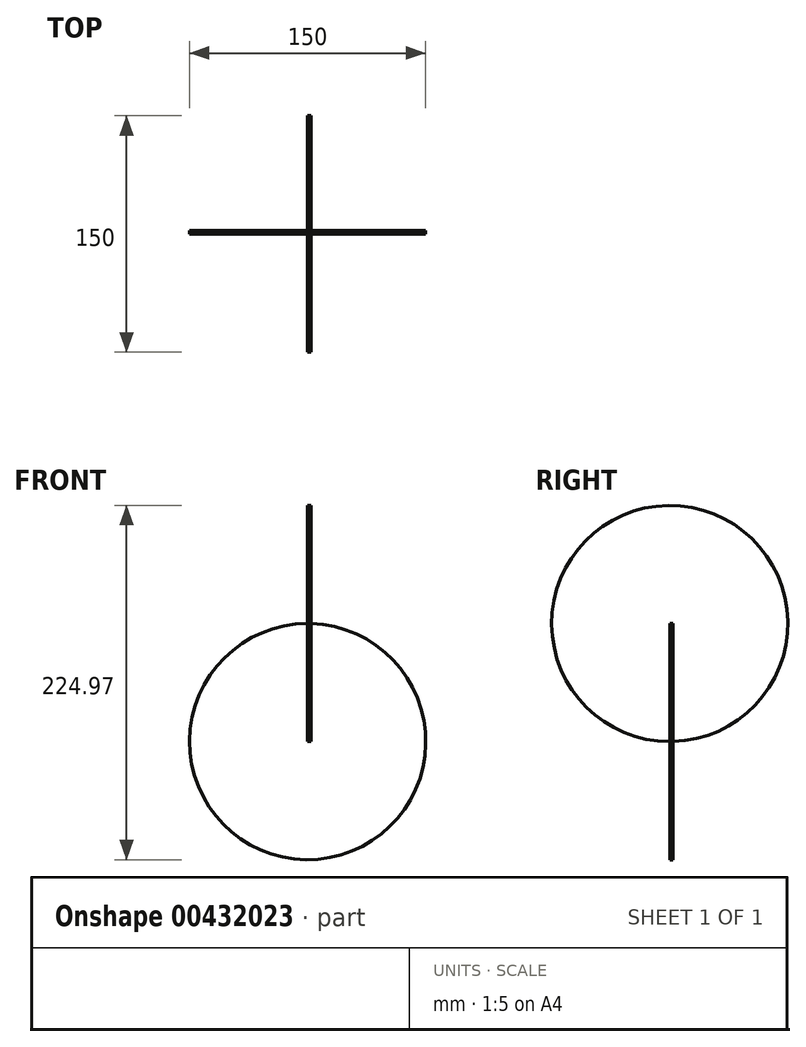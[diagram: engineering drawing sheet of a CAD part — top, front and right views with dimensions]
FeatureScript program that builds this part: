
annotation { "Feature Type Name" : "Feature", "Feature Type Description" : "" }
export const myFeature = defineFeature(function(context is Context, id is Id, definition is map)
    precondition{}
    {
        {
            var Q0;
            Q0=qCreatedBy(makeId("Front.planeOp"),FACE);
            var sketch = newSketch(context, id + "F0", { "sketchPlane" : qUnion([Q0])});
            skCircle(sketch, "E0", {"center": v(0, 0) * mm, "radius": 75 * mm});
            skSolve(sketch);
        }
        {
            var Q0;
            Q0 = qSketchRegion(id + "F0", true);
            var Q1;
            Q1=makeQuery(id+"F0.imprint","IMPRINT",FACE,{"disambiguationData":[TD([[makeQuery(id+"F0.imprint","IMPRINT",EDGE,{"derivedFrom":sQuery(id+"F0.wireOp",EDGE,"E0")}),1.0]])]});
            extrude(context, id + "F1", {"entities" : qUnion([Q0, Q1]), "depth" : 2 * mm});
        }
        {
            var Q0;
            Q0=qCreatedBy(makeId("Right.planeOp"),FACE);
            var sketch = newSketch(context, id + "F2", { "sketchPlane" : qUnion([Q0])});
            skCircle(sketch, "E1", {"center": v(-2, 74.97) * mm, "radius": 75 * mm});
            skSolve(sketch);
        }
        {
            var Q0;
            Q0 = qSketchRegion(id + "F2", true);
            var Q1;
            Q1=makeQuery(id+"F2.imprint","IMPRINT",FACE,{"disambiguationData":[TD([[makeQuery(id+"F2.imprint","IMPRINT",EDGE,{"derivedFrom":sQuery(id+"F2.wireOp",EDGE,"E1")}),1.0]])]});
            extrude(context, id + "F3", {"entities" : qUnion([Q0, Q1]), "operationType" : NewBodyOperationType.ADD, "depth" : 2 * mm});
        }
    });
